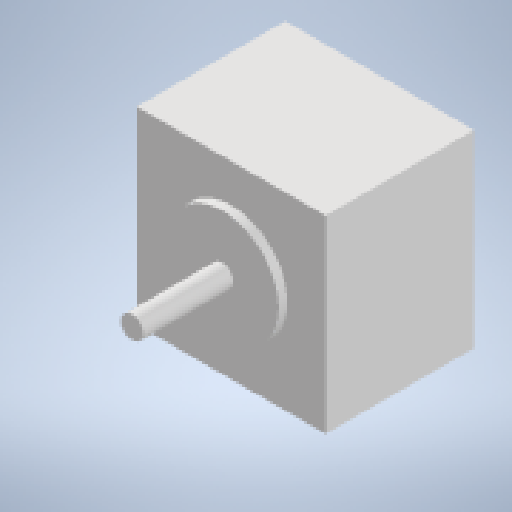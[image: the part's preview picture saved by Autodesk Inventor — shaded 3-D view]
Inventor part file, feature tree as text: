
AUTODESK INVENTOR PART (.ipt)
format: ipt  version: 2023 (Build 270158000, 158)  size: 139,776 bytes
history: native  units: mm
features: extrude x3, sketch x3, other x3, reference x1
ambient origin geometry x8: Origin, YZ Plane, XZ Plane, XY Plane, X Axis, Y Axis, Z Axis, Center Point
bodies: Solid1 (feature_tree)
feature tree (10):
  extrude  "Extrusion1"  Depth=42.0mm
  extrude  "Extrusion2"  Depth=33.0mm
  extrude  "Extrusion3"  Depth=20.0mm
  sketch  "Sketch1"  dims[d0=42.0mm d1=42.0mm]
  reference  "Reference1"
  sketch  "Sketch2"  dims[d2=33.0mm d3=0.0mm d4=25.0mm]
  sketch  "Sketch3"  dims[d5=2.0mm d6=0.0mm d7=5.0mm d8=20.0mm d9=0.0mm]
  other  "<userpath>\OneDrive\Namizje\school\4. letnik\Matura\Izdelovanje\3D model\3D_skenner.iam"
  other  "3D_skenner.iam"
  other  "Ogrodje_spodaj_1:1"
